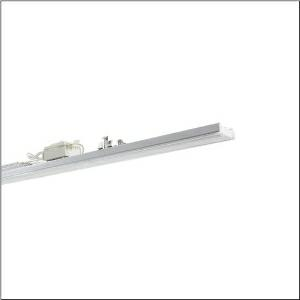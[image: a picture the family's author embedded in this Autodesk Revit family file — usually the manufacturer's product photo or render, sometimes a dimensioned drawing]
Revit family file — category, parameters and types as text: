
# Revit family: licross_r__11_recessed_ho_51tl12dn4exm3c_4ac0
name_source: partatom
category: Lighting Fixtures
units: mm (PartAtom-declared; Revit-internal decimal feet)

## family parameters
Cut with Voids When Loaded = No
Host = Face
Light Source = No
Part Type = Normal
Room Calculation Point = No
Round Connector Dimension = Use Diameter
Shared = No

## types (1)
- --- (1 x LED, 1000 lm, 7.2 W, 4000K)
    Apparent Load = 7 VA
    CIE Flux Codes = 66 91 98 100 100
    Color Rendering = 80
    Color Temperature = 4000K
    Default Elevation = 1800 mm
    Description = Licross® 11 Recessed HO, luminaire insert, of sheet steel, coil coated, white, length: 1.500mm, width: 66mm, height: 67mm, LED rated luminous flux: 14.030lm, light colour: 840, control gear: DALI 2 (for two DALI lines), with plug, 6-pole, with phase selection, for trunking rail, 14-core, mains connection: 220..240V, AC, 50/60Hz, rated input power: 81W, for trunking rail, 14-core, internal wiring halogen-free, for emergency light function, converter,control gear: single battery element, battery: LiFePO4, 9Ah, primary optical cover: cover, of PMMA, light emission: direct distribution, primary light characteristic: symmetric, protection rating (complete): IP40, insulation class (complete): insulation class I (protective earthing), certification: CE, UKCA, protection symbol: D if used in an environment without relevant dust loads with corresponding accessories, impact resistance: IK06, permissible ambient temperature for indoor applications: +5..+30°C, standard: EN 60598-2-22, LABS conformity tested according to VDMA 24364:2018-05, reducing of maximum allowable ambient temperature of 5°C with ceiling mounting, corresponds to IFS (International Featured Standards) requirements for safety and quality in the food industry, packaging unit: 1 piece
    Height = 58 mm
    Lamp = 1 x LED
    Lamp Light Flux = 1000 lm
    Lamp Power = 7.2 W
    Lamp count = 1
    Length = 1500 mm
    Luminous efficacy = 139 lm/W
    Manufacturer = Siteco
    ModVariant = No
    Model = 51TL12DN4EXM3C
    Mounting Place = Ceiling
    Mounting Type = Pendant
    Number of Poles = 1
    OnlyDefault = Yes
    Power Factor = 1
    Product Name = Licross® 11 Recessed HO
    Product group = luminaire insert | ceiling pendant
    ProductGroupID = 902
    Protection Class = Protection class I
    Protection Degree = IP 40
    RLX_Detail_Level = 1
    RLX_Emergency_Light_Flux = 0 lm
    RLX_Emergency_Type = 0
    RLX_Emergency_Type_DB = No
    RlxData = <blob elided: 24961 chars, md5=12346e73>
    Socket = socket
    Standby Power = 0 W
    System Light Flux = 1000 lm
    System Power = 7 W
    Type Comments = : emergency light operation: 3 h
    Type Image = l_1296930.jpg
    URL = http://relux.com
    VarID = @adj_111507
    Voltage = 0 V
    Weight = 0.00 kg
    Width = 66 mm

## geometry (parser evidence)
native form markers: Blend x4, Sweep x10
no freeform markers — native parametric forms only
